# Revit family: Haworth_PopUp_Rectangle_Table_AP_PRELIMINARY
name_source: partatom
category: Furniture
revit_build: Autodesk Revit 2018 (Build: 20170223_1515(x64)
units: mm (PartAtom-declared; Revit-internal decimal feet)

## family parameters
Always vertical = Yes
Cut with Voids When Loaded = No
OmniClass Number = 23.40.70.14.64.21
OmniClass Title = Systems Furniture
Room Calculation Point = No
Shared = No
Work Plane-Based = No

## types (6) — shared parameters
Assembly Code = E2020200
Caster Finish = Haworth _ Paint _ Metallic Gunmetal
Casters = Yes
Custom Size = No
Description = Haworth - PopUp - Rectangle Table - AP Wood
Glides = No
Manufacturer = Haworth
Max. Depth = 750 mm  [stored 2.46063 ft]
Max. Width = 1800 mm  [stored 5.90551 ft]
Min. Depth = 450 mm  [stored 1.47638 ft]
Min. Width = 1200 mm
Min/Max Depth = 450, 600, 750 mm
Min/Max Height = 915, 1050 mm
Min/Max Width = 1200, 1400, 1500, 1600, 1800 mm
Model = WOPURTXXXX
Revision Number = 1
Size = Verify Final Dim. w/ Haworth
Support Offset = 150 mm
Table Thickness = 30 mm  [stored 0.0984252 ft]
URL = https://www.haworth.com
URL - Product = https://www.haworth.com
Warranty = http://www.haworth.com

## per-type parameters (varying)
| type | Actual Depth | Actual Height | Actual Width | Depth | High | Large | Leg Height | Low | Plate Depth | Plate Length | Plate Width | Small | Width |
| 1800 x 750 x 1050 | 750 mm  [stored 2.46063 ft] | 1050 mm | 1800 mm  [stored 5.90551 ft] | 750 mm  [stored 2.46063 ft] | Yes | Yes | 1020 mm  [stored 3.34646 ft] | No | 380 mm  [stored 1.24672 ft] | 1500 mm  [stored 4.92126 ft] | 190 mm | No | 1800 mm  [stored 5.90551 ft] |
| 1200 x 750 x 915 | 750 mm  [stored 2.46063 ft] | 915 mm  [stored 3.00197 ft] | 1200 mm | 750 mm  [stored 2.46063 ft] | No | Yes | 885 mm  [stored 2.90354 ft] | Yes | 380 mm  [stored 1.24672 ft] | 900 mm  [stored 2.95276 ft] | 190 mm | No | 1200 mm |
| 1600 x 600 x 915 | 600 mm | 915 mm  [stored 3.00197 ft] | 1600 mm  [stored 5.24934 ft] | 600 mm | No | Yes | 885 mm  [stored 2.90354 ft] | Yes | 230 mm | 1300 mm  [stored 4.26509 ft] | 115 mm  [stored 0.377297 ft] | No | 1600 mm  [stored 5.24934 ft] |
| 1400 x 600 x 1050 | 600 mm | 1050 mm | 1400 mm  [stored 4.59318 ft] | 600 mm | Yes | Yes | 1020 mm  [stored 3.34646 ft] | No | 230 mm | 1100 mm | 115 mm  [stored 0.377297 ft] | No | 1400 mm  [stored 4.59318 ft] |
| 1500 x 450 x 915 | 450 mm  [stored 1.47638 ft] | 915 mm  [stored 3.00197 ft] | 1500 mm  [stored 4.92126 ft] | 450 mm  [stored 1.47638 ft] | No | No | 885 mm  [stored 2.90354 ft] | Yes | 80 mm | 1200 mm | 65 mm  [stored 0.213255 ft] | Yes | 1500 mm  [stored 4.92126 ft] |
| 1800 x 450 x 1050 | 450 mm  [stored 1.47638 ft] | 1050 mm | 1800 mm  [stored 5.90551 ft] | 450 mm  [stored 1.47638 ft] | Yes | No | 1020 mm  [stored 3.34646 ft] | No | 80 mm | 1500 mm  [stored 4.92126 ft] | 65 mm  [stored 0.213255 ft] | Yes | 1800 mm  [stored 5.90551 ft] |

note: [stored X ft] marks values corroborated as IEEE doubles in the binary element streams (Revit-internal decimal feet)

## geometry (parser evidence)
native form markers: Sweep x10
no freeform markers — native parametric forms only
